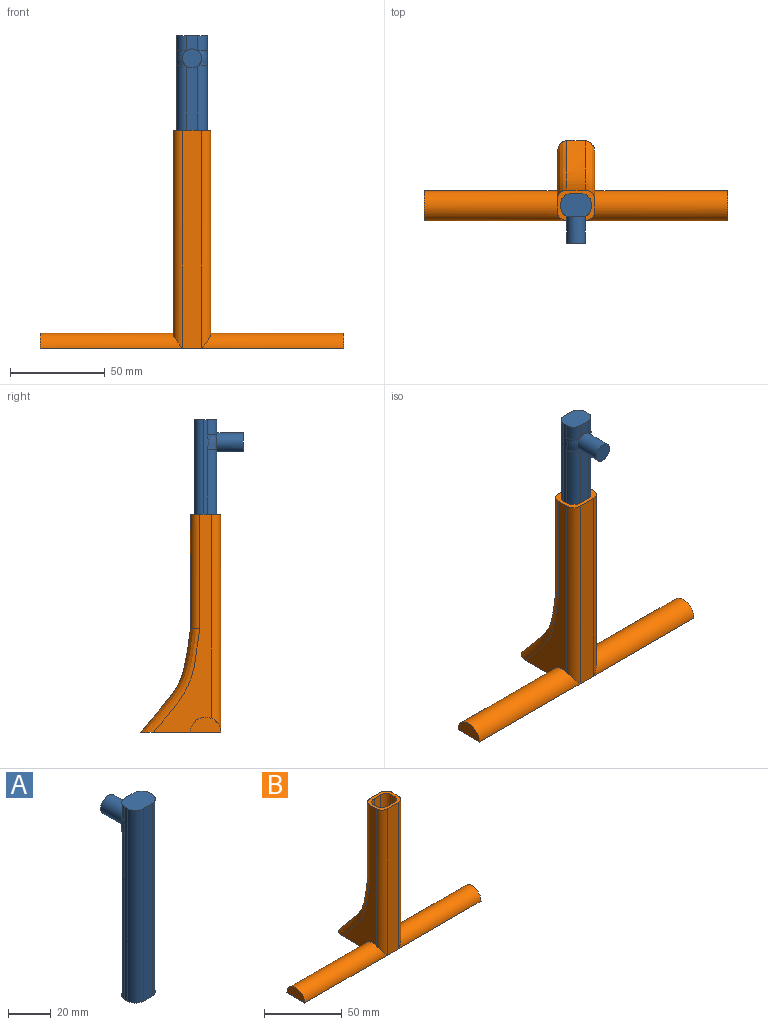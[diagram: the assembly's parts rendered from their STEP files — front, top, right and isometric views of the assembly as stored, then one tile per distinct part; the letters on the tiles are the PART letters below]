
ASSEMBLY  parts=2 mates=1
PART A: 24 faces, bbox 16x26x110 mm
  f0: plane 94x6mm, normal (0,1,0), area 559.9mm2, adj f1,f14,f16,f21
  f1: plane 16x12mm, normal (0,0,-1), area 74.5mm2, adj f0,f3,f4,f5,f7,f8,f9,f10
  f2: plane 8x6mm, normal (0,1,0), area 43.9mm2, adj f6,f14,f18,f23
  f3: plane 110x2.42mm, normal (-1,0,0), area 221.6mm2, adj f1,f6,f16,f17,f18,f19
  f4: plane 110x6mm, normal (0,-1,0), area 660mm2, adj f1,f6,f19,f20
  f5: plane 110x2.42mm, normal (1,0,0), area 221.6mm2, adj f1,f6,f20,f21,f22,f23
  f6: plane 16x12mm, normal (0,0,1), area 170.5mm2, adj f2,f3,f4,f5,f18,f19,f20,f23
  f7: plane 108x12mm, normal (0,-1,0), area 1217.5mm2, adj f1,f8,f10,f11,f13
  f8: plane 108x8mm, normal (1,0,0), area 864mm2, adj f1,f7,f9,f11
  f9: plane 108x12mm, normal (0,1,0), area 1296mm2, adj f1,f8,f10,f11
  f10: plane 108x8mm, normal (-1,0,0), area 864mm2, adj f1,f7,f9,f11
  f11: plane 12x8mm, normal (0,0,-1), area 96mm2, adj f7,f8,f9,f10
  f12: plane 10x10mm, normal (0,-1,0), area 78.5mm2, adj f13
  f13: cylinder r=5mm len=10mm, axis (0,-1,0), area 125.7mm2, adj f7,f12
  f14: cylinder r=5mm len=14mm, axis (0,-1,0), area 439.8mm2, adj f0,f2,f15,f17,f22
  f15: plane 10x10mm, normal (0,1,0), area 78.5mm2, adj f14
  f16: cylinder r=5mm len=94mm, axis (0,0,1), area 738.3mm2, adj f0,f1,f3,f17
  f17: bspline ~8.77x5.26mm, area 51.8mm2, adj f3,f14,f16,f18
  f18: cylinder r=5mm len=8mm, axis (0,0,1), area 62.8mm2, adj f2,f3,f6,f17
  f19: cylinder r=5mm len=110mm, axis (0,0,-1), area 863.9mm2, adj f1,f3,f4,f6
  f20: cylinder r=5mm len=110mm, axis (0,0,1), area 863.9mm2, adj f1,f4,f5,f6
  f21: cylinder r=5mm len=94mm, axis (0,0,-1), area 738.3mm2, adj f0,f1,f5,f22
  f22: bspline ~8.77x5.25mm, area 51.8mm2, adj f5,f14,f21,f23
  f23: cylinder r=5mm len=8mm, axis (0,0,-1), area 62.8mm2, adj f2,f5,f6,f22
PART B: 26 faces, bbox 161.7x46.8x123.1 mm
  f0: plane 20x16mm, normal (0,0,1), area 128mm2, adj f1,f2,f3,f4,f6,f7,f8,f9
  f1: plane 60.06x10mm, normal (0,1,0), area 600.6mm2, adj f0,f15,f16,f18
  f2: plane 115x30.66mm, normal (-1,0,0), area 1047.1mm2, adj f0,f5,f13,f18,f19,f24
  f3: plane 115x10mm, normal (0,-1,0), area 1150mm2, adj f0,f5,f24,f25
  f4: plane 115x30.66mm, normal (1,0,0), area 1047.1mm2, adj f0,f5,f12,f16,f17,f25
  f5: plane 161.67x44mm, normal (0,0,-1), area 3072.3mm2, adj f2,f3,f4,f11,f12,f13,f14,f15
  f6: plane 109.71x6mm, normal (0,-1,0), area 658.3mm2, adj f0,f10,f21,f23
  f7: plane 107.06x2mm, normal (1,0,0), area 214mm2, adj f0,f10,f22,f23
  f8: plane 109.71x6mm, normal (0,1,0), area 658.3mm2, adj f0,f10,f20,f22
  f9: plane 107.06x2mm, normal (-1,0,0), area 214mm2, adj f0,f10,f20,f21
  f10: cylinder r=8mm len=16mm, axis (1,0,0), area 189.3mm2, adj f6,f7,f8,f9,f20,f21,f22,f23
  f11: plane 16x8mm, normal (1,0,0), area 100.5mm2, adj f5,f12
  f12: cylinder r=8mm len=75mm, axis (1,0,0), area 1783mm2, adj f4,f5,f11,f25
  f13: cylinder r=8mm len=75mm, axis (1,0,0), area 1783mm2, adj f2,f5,f14,f24
  f14: plane 16x8mm, normal (-1,0,0), area 100.5mm2, adj f5,f13
  f15: extruded ~54.94x26.33mm, area 627.3mm2, adj f1,f5,f17,f19
  f16: cylinder r=5mm len=60.34mm, axis (0,0,-1), area 472.8mm2, adj f0,f1,f4,f17
  f17: bspline ~66.61x34.65mm, area 485.1mm2, adj f4,f5,f15,f16
  f18: cylinder r=5mm len=60.34mm, axis (0,0,1), area 472.8mm2, adj f0,f1,f2,f19
  f19: bspline ~66.61x34.65mm, area 485.1mm2, adj f2,f5,f15,f18
  f20: cylinder r=5mm len=109.71mm, axis (0,0,-1), area 851.3mm2, adj f0,f8,f9,f10
  f21: cylinder r=5mm len=109.71mm, axis (0,0,1), area 851.3mm2, adj f0,f6,f9,f10
  f22: cylinder r=5mm len=109.71mm, axis (0,0,1), area 851.3mm2, adj f0,f7,f8,f10
  f23: cylinder r=5mm len=109.71mm, axis (0,0,-1), area 851.3mm2, adj f0,f6,f7,f10
  f24: cylinder r=5mm len=115mm, axis (0,0,-1), area 874.1mm2, adj f0,f2,f3,f13
  f25: cylinder r=5mm len=115mm, axis (0,0,1), area 874.1mm2, adj f0,f3,f4,f12
PLACE A rot(axis=(0,0,1),180deg) t=(-146.05,-99.76,155.79)mm
PLACE B rot(axis=(0.36,-0.82,-0.44),0deg) t=(-146.05,-99.76,115.79)mm fixed
MATE slider A.f1 <-> B.f0  axis (0,0,-1) through (-146.05,-99.76,155.79)mm
